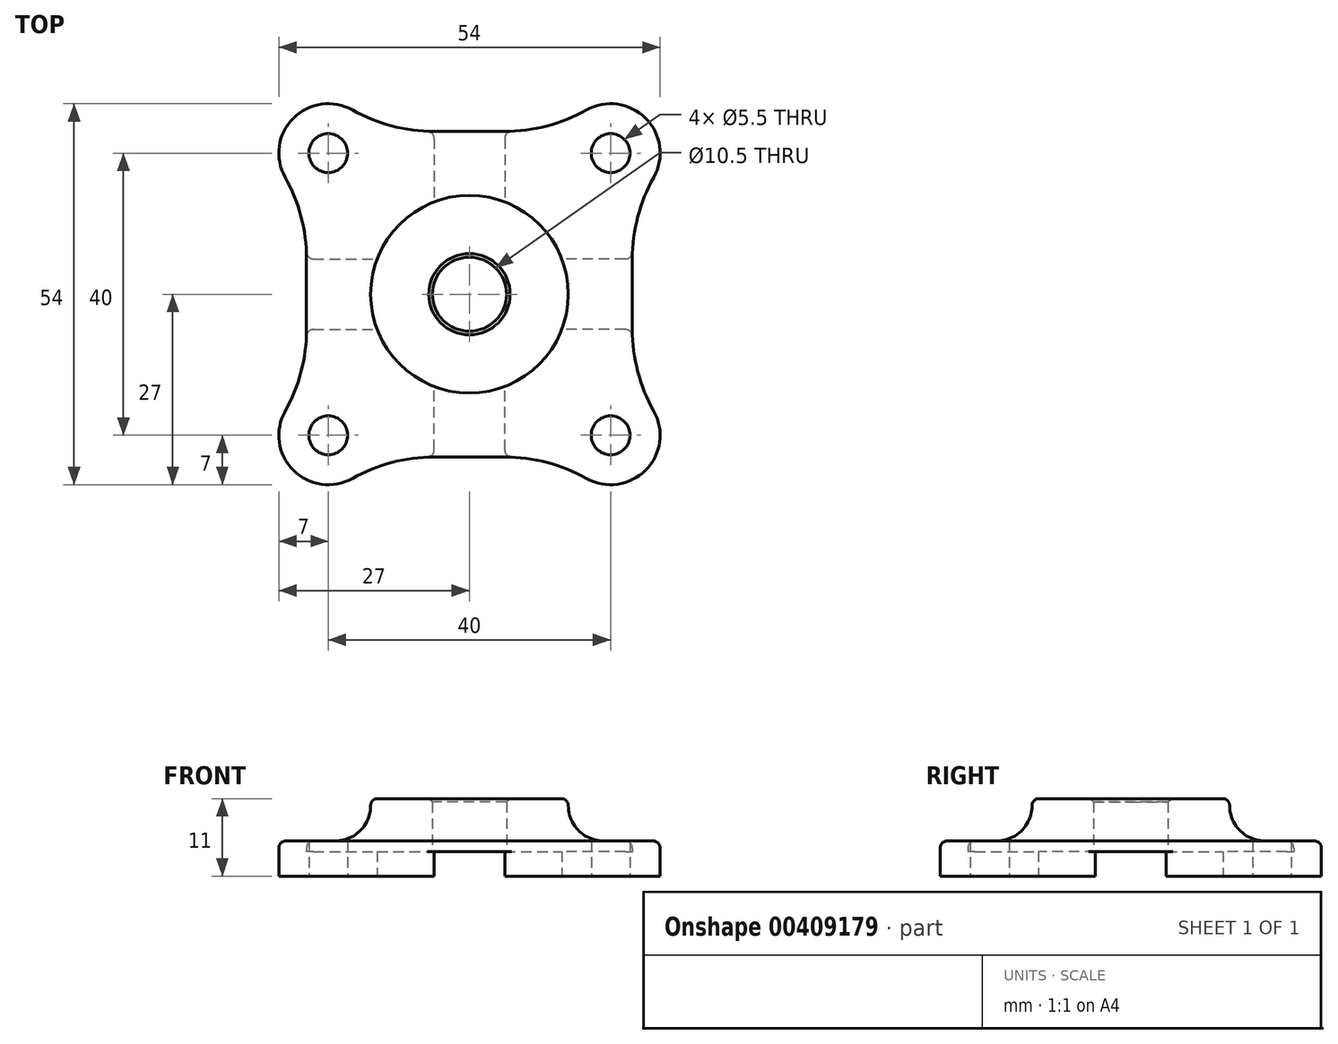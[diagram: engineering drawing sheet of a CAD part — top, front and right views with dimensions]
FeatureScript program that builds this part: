
annotation { "Feature Type Name" : "Feature", "Feature Type Description" : "" }
export const myFeature = defineFeature(function(context is Context, id is Id, definition is map)
    precondition{}
    {
        {
            var Q0;
            Q0=qCreatedBy(makeId("Top.planeOp"),FACE);
            var sketch = newSketch(context, id + "F0", { "sketchPlane" : qUnion([Q0])});
            skCircle(sketch, "E0", {"center": v(0, 0) * mm, "radius": 14 * mm});
            skCircle(sketch, "E1", {"center": v(0, 0) * mm, "radius": 5.25 * mm});
            skCircle(sketch, "E2", {"center": v(0, 0) * mm, "radius": 5 * mm});
            skCircle(sketch, "E3", {"center": v(0, 0) * mm, "radius": 13.5 * mm});
            skCircle(sketch, "E4", {"center": v(-20, 20) * mm, "radius": 2.75 * mm});
            skArc(sketch, "E5", {"start": v(-24.95, 24.95) * mm, "mid": v(-26.93, 20.96) * mm, "end": v(-26.1, 16.57) * mm});
            skLineSegment(sketch, "E6", {"start": v(-23.08, 5) * mm, "end": v(-13.08, 5) * mm});
            skArc(sketch, "E7", {"start": v(-26.1, 16.57) * mm, "mid": v(-23.85, 10.98) * mm, "end": v(-23.08, 5) * mm});
            skLineSegment(sketch, "E8", {"start": v(-20, 20) * mm, "end": v(0, 0) * mm, "construction": true});
            skLineSegment(sketch, "E9", {"start": v(-23.08, 5) * mm, "end": v(-23.08, 0) * mm});
            skArc(sketch, "E10.MirrorCS", {"start": v(-24.95, 24.95) * mm, "mid": v(-20.96, 26.93) * mm, "end": v(-16.57, 26.1) * mm});
            skArc(sketch, "E11.MirrorCS", {"start": v(-16.57, 26.1) * mm, "mid": v(-10.98, 23.85) * mm, "end": v(-5, 23.08) * mm});
            skLineSegment(sketch, "E12.MirrorCS", {"start": v(-5, 23.08) * mm, "end": v(-5, 13.08) * mm});
            skLineSegment(sketch, "E13.MirrorCS", {"start": v(-5, 23.08) * mm, "end": v(0, 23.08) * mm});
            skArc(sketch, "E14.1.0", {"start": v(-26.1, -16.57) * mm, "mid": v(-23.85, -10.98) * mm, "end": v(-23.08, -5) * mm});
            skLineSegment(sketch, "E14.1.1", {"start": v(-5, -23.08) * mm, "end": v(-5, -13.08) * mm});
            skArc(sketch, "E14.1.2", {"start": v(-24.95, -24.95) * mm, "mid": v(-26.93, -20.96) * mm, "end": v(-26.1, -16.57) * mm});
            skArc(sketch, "E14.1.3", {"start": v(-24.95, -24.95) * mm, "mid": v(-20.96, -26.93) * mm, "end": v(-16.57, -26.1) * mm});
            skLineSegment(sketch, "E14.1.4", {"start": v(-5, -23.08) * mm, "end": v(0, -23.08) * mm});
            skCircle(sketch, "E14.1.5", {"center": v(-20, -20) * mm, "radius": 2.75 * mm});
            skLineSegment(sketch, "E14.1.7", {"start": v(-23.08, -5) * mm, "end": v(-23.08, 0) * mm});
            skLineSegment(sketch, "E14.1.8", {"start": v(-23.08, -5) * mm, "end": v(-13.08, -5) * mm});
            skArc(sketch, "E14.1.9", {"start": v(-16.57, -26.1) * mm, "mid": v(-10.98, -23.85) * mm, "end": v(-5, -23.08) * mm});
            skLineSegment(sketch, "E14.1.10", {"start": v(-20, -20) * mm, "end": v(0, 0) * mm, "construction": true});
            skArc(sketch, "E14.2.0", {"start": v(16.57, -26.1) * mm, "mid": v(10.98, -23.85) * mm, "end": v(5, -23.08) * mm});
            skLineSegment(sketch, "E14.2.1", {"start": v(23.08, -5) * mm, "end": v(13.08, -5) * mm});
            skArc(sketch, "E14.2.2", {"start": v(24.95, -24.95) * mm, "mid": v(20.96, -26.93) * mm, "end": v(16.57, -26.1) * mm});
            skArc(sketch, "E14.2.3", {"start": v(24.95, -24.95) * mm, "mid": v(26.93, -20.96) * mm, "end": v(26.1, -16.57) * mm});
            skLineSegment(sketch, "E14.2.4", {"start": v(23.08, -5) * mm, "end": v(23.08, 0) * mm});
            skCircle(sketch, "E14.2.5", {"center": v(20, -20) * mm, "radius": 2.75 * mm});
            skLineSegment(sketch, "E14.2.7", {"start": v(5, -23.08) * mm, "end": v(0, -23.08) * mm});
            skLineSegment(sketch, "E14.2.8", {"start": v(5, -23.08) * mm, "end": v(5, -13.08) * mm});
            skArc(sketch, "E14.2.9", {"start": v(26.1, -16.57) * mm, "mid": v(23.85, -10.98) * mm, "end": v(23.08, -5) * mm});
            skLineSegment(sketch, "E14.2.10", {"start": v(20, -20) * mm, "end": v(0, 0) * mm, "construction": true});
            skArc(sketch, "E14.3.0", {"start": v(26.1, 16.57) * mm, "mid": v(23.85, 10.98) * mm, "end": v(23.08, 5) * mm});
            skLineSegment(sketch, "E14.3.1", {"start": v(5, 23.08) * mm, "end": v(5, 13.08) * mm});
            skArc(sketch, "E14.3.2", {"start": v(24.95, 24.95) * mm, "mid": v(26.93, 20.96) * mm, "end": v(26.1, 16.57) * mm});
            skArc(sketch, "E14.3.3", {"start": v(24.95, 24.95) * mm, "mid": v(20.96, 26.93) * mm, "end": v(16.57, 26.1) * mm});
            skLineSegment(sketch, "E14.3.4", {"start": v(5, 23.08) * mm, "end": v(0, 23.08) * mm});
            skCircle(sketch, "E14.3.5", {"center": v(20, 20) * mm, "radius": 2.75 * mm});
            skLineSegment(sketch, "E14.3.7", {"start": v(23.08, 5) * mm, "end": v(23.08, 0) * mm});
            skLineSegment(sketch, "E14.3.8", {"start": v(23.08, 5) * mm, "end": v(13.08, 5) * mm});
            skArc(sketch, "E14.3.9", {"start": v(16.57, 26.1) * mm, "mid": v(10.98, 23.85) * mm, "end": v(5, 23.08) * mm});
            skLineSegment(sketch, "E14.3.10", {"start": v(20, 20) * mm, "end": v(0, 0) * mm, "construction": true});
            skSolve(sketch);
        }
        {
            var Q0;
            {var subQ0=sQuery(id+"F0.wireOp",EDGE,"E14.2.1");Q0=makeQuery(id+"F0.imprint","IMPRINT",FACE,{"disambiguationData":[TD([[makeQuery(id+"F0.imprint","IMPRINT",EDGE,{"derivedFrom":subQ0}),-1.0]])]});}
            var Q1;
            Q1=makeQuery(id+"F0.imprint","IMPRINT",FACE,{"disambiguationData":[TD([[makeQuery(id+"F0.imprint","IMPRINT",EDGE,{"derivedFrom":sQuery(id+"F0.wireOp",EDGE,"E14.3.0")}),-1.0]])]});
            var Q2;
            Q2=makeQuery(id+"F0.imprint","IMPRINT",FACE,{"disambiguationData":[TD([[makeQuery(id+"F0.imprint","IMPRINT",EDGE,{"derivedFrom":sQuery(id+"F0.wireOp",EDGE,"E14.2.0")}),-1.0]])]});
            var Q3;
            Q3=makeQuery(id+"F0.imprint","IMPRINT",FACE,{"disambiguationData":[TD([[makeQuery(id+"F0.imprint","IMPRINT",EDGE,{"derivedFrom":sQuery(id+"F0.wireOp",EDGE,"E4")}),-1.0]])]});
            var Q4;
            Q4=makeQuery(id+"F0.imprint","IMPRINT",FACE,{"disambiguationData":[TD([[makeQuery(id+"F0.imprint","IMPRINT",EDGE,{"derivedFrom":sQuery(id+"F0.wireOp",EDGE,"E3")}),-1.0]])]});
            var Q5;
            Q5=makeQuery(id+"F0.imprint","IMPRINT",FACE,{"disambiguationData":[TD([[makeQuery(id+"F0.imprint","IMPRINT",EDGE,{"derivedFrom":sQuery(id+"F0.wireOp",EDGE,"E14.1.0")}),-1.0]])]});
            var Q6;
            {var subQ0=sQuery(id+"F0.wireOp",EDGE,"E14.1.1");Q6=makeQuery(id+"F0.imprint","IMPRINT",FACE,{"disambiguationData":[TD([[makeQuery(id+"F0.imprint","IMPRINT",EDGE,{"derivedFrom":subQ0}),-1.0]])]});}
            var Q7;
            Q7=makeQuery(id+"F0.imprint","IMPRINT",FACE,{"disambiguationData":[TD([[makeQuery(id+"F0.imprint","IMPRINT",EDGE,{"derivedFrom":sQuery(id+"F0.wireOp",EDGE,"E1")}),-1.0]])]});
            var Q8;
            {var subQ0=sQuery(id+"F0.wireOp",EDGE,"E6");Q8=makeQuery(id+"F0.imprint","IMPRINT",FACE,{"disambiguationData":[TD([[makeQuery(id+"F0.imprint","IMPRINT",EDGE,{"derivedFrom":subQ0}),-1.0]])]});}
            var Q9;
            {var subQ1=sQuery(id+"F0.wireOp",EDGE,"E12.MirrorCS");Q9=makeQuery(id+"F0.imprint","IMPRINT",FACE,{"disambiguationData":[TD([[makeQuery(id+"F0.imprint","IMPRINT",EDGE,{"derivedFrom":subQ1}),1.0]])]});}
            extrude(context, id + "F1", {"entities" : qUnion([Q0, Q1, Q2, Q3, Q4, Q5, Q6, Q7, Q8, Q9]), "depth" : 3 * mm, "offsetDistance" : 25 * mm});
        }
        {
            var Q0;
            Q0=makeQuery(id+"F0.imprint","IMPRINT",FACE,{"disambiguationData":[TD([[makeQuery(id+"F0.imprint","IMPRINT",EDGE,{"derivedFrom":sQuery(id+"F0.wireOp",EDGE,"E0")}),1.0]])]});
            var Q1;
            Q1=makeQuery(id+"F0.imprint","IMPRINT",FACE,{"disambiguationData":[TD([[makeQuery(id+"F0.imprint","IMPRINT",EDGE,{"derivedFrom":sQuery(id+"F0.wireOp",EDGE,"E1")}),-1.0]])]});
            extrude(context, id + "F2", {"entities" : qUnion([Q0, Q1]), "operationType" : NewBodyOperationType.ADD, "depth" : 9 * mm});
        }
        {
            var Q0;
            Q0=makeQuery(id+"F0.imprint","IMPRINT",FACE,{"disambiguationData":[TD([[makeQuery(id+"F0.imprint","IMPRINT",EDGE,{"derivedFrom":sQuery(id+"F0.wireOp",EDGE,"E1")}),-1.0]])]});
            var Q1;
            {var subQ0=sQuery(id+"F0.wireOp",EDGE,"5FznAjd5-Rlev-DzMA-E21E-VBbVsZXluKNu");Q1=makeQuery(id+"F0.imprint","IMPRINT",FACE,{"disambiguationData":[TD([[makeQuery(id+"F0.imprint","IMPRINT",EDGE,{"derivedFrom":subQ0}),1.0]])]});}
            var Q2;
            Q2=makeQuery(id+"F0.imprint","IMPRINT",FACE,{"disambiguationData":[TD([[makeQuery(id+"F0.imprint","IMPRINT",EDGE,{"derivedFrom":sQuery(id+"F0.wireOp",EDGE,"E3")}),-1.0]])]});
            var Q3;
            {var subQ1=sQuery(id+"F0.wireOp",EDGE,"bf5245d6-79ee-4a8b-a03c-ecbf48f2092a0.MirrorCS");Q3=makeQuery(id+"F0.imprint","IMPRINT",FACE,{"disambiguationData":[TD([[makeQuery(id+"F0.imprint","IMPRINT",EDGE,{"derivedFrom":subQ1}),-1.0]])]});}
            var Q4;
            {var subQ0=sQuery(id+"F0.wireOp",EDGE,"E14.1.1");Q4=makeQuery(id+"F0.imprint","IMPRINT",FACE,{"disambiguationData":[TD([[makeQuery(id+"F0.imprint","IMPRINT",EDGE,{"derivedFrom":subQ0}),-1.0]])]});}
            var Q5;
            {var subQ0=sQuery(id+"F0.wireOp",EDGE,"E6");Q5=makeQuery(id+"F0.imprint","IMPRINT",FACE,{"disambiguationData":[TD([[makeQuery(id+"F0.imprint","IMPRINT",EDGE,{"derivedFrom":subQ0}),-1.0]])]});}
            var Q6;
            {var subQ0=sQuery(id+"F0.wireOp",EDGE,"E14.2.1");Q6=makeQuery(id+"F0.imprint","IMPRINT",FACE,{"disambiguationData":[TD([[makeQuery(id+"F0.imprint","IMPRINT",EDGE,{"derivedFrom":subQ0}),-1.0]])]});}
            var Q7;
            {var subQ1=sQuery(id+"F0.wireOp",EDGE,"E12.MirrorCS");Q7=makeQuery(id+"F0.imprint","IMPRINT",FACE,{"disambiguationData":[TD([[makeQuery(id+"F0.imprint","IMPRINT",EDGE,{"derivedFrom":subQ1}),1.0]])]});}
            extrude(context, id + "F3", {"entities" : qUnion([Q0, Q1, Q2, Q3, Q4, Q5, Q6, Q7]), "operationType" : NewBodyOperationType.REMOVE, "depth" : 1.5 * mm, "offsetDistance" : 25 * mm});
        }
        {
            var Q0;
            Q0=makeQuery(id+"F0.imprint","IMPRINT",FACE,{"disambiguationData":[TD([[makeQuery(id+"F0.imprint","IMPRINT",EDGE,{"derivedFrom":sQuery(id+"F0.wireOp",EDGE,"E14.1.0")}),-1.0]])]});
            var Q1;
            {var subQ0=sQuery(id+"F0.wireOp",EDGE,"E14.1.1");Q1=makeQuery(id+"F0.imprint","IMPRINT",FACE,{"disambiguationData":[TD([[makeQuery(id+"F0.imprint","IMPRINT",EDGE,{"derivedFrom":subQ0}),-1.0]])]});}
            var Q2;
            Q2=makeQuery(id+"F0.imprint","IMPRINT",FACE,{"disambiguationData":[TD([[makeQuery(id+"F0.imprint","IMPRINT",EDGE,{"derivedFrom":sQuery(id+"F0.wireOp",EDGE,"E14.2.0")}),-1.0]])]});
            var Q3;
            {var subQ0=sQuery(id+"F0.wireOp",EDGE,"E14.2.1");Q3=makeQuery(id+"F0.imprint","IMPRINT",FACE,{"disambiguationData":[TD([[makeQuery(id+"F0.imprint","IMPRINT",EDGE,{"derivedFrom":subQ0}),-1.0]])]});}
            var Q4;
            Q4=makeQuery(id+"F0.imprint","IMPRINT",FACE,{"disambiguationData":[TD([[makeQuery(id+"F0.imprint","IMPRINT",EDGE,{"derivedFrom":sQuery(id+"F0.wireOp",EDGE,"E14.3.0")}),-1.0]])]});
            var Q5;
            {var subQ1=sQuery(id+"F0.wireOp",EDGE,"E12.MirrorCS");Q5=makeQuery(id+"F0.imprint","IMPRINT",FACE,{"disambiguationData":[TD([[makeQuery(id+"F0.imprint","IMPRINT",EDGE,{"derivedFrom":subQ1}),1.0]])]});}
            var Q6;
            Q6=makeQuery(id+"F0.imprint","IMPRINT",FACE,{"disambiguationData":[TD([[makeQuery(id+"F0.imprint","IMPRINT",EDGE,{"derivedFrom":sQuery(id+"F0.wireOp",EDGE,"E4")}),-1.0]])]});
            var Q7;
            {var subQ0=sQuery(id+"F0.wireOp",EDGE,"E6");Q7=makeQuery(id+"F0.imprint","IMPRINT",FACE,{"disambiguationData":[TD([[makeQuery(id+"F0.imprint","IMPRINT",EDGE,{"derivedFrom":subQ0}),-1.0]])]});}
            var Q8;
            Q8=makeQuery(id+"F0.imprint","IMPRINT",FACE,{"disambiguationData":[TD([[makeQuery(id+"F0.imprint","IMPRINT",EDGE,{"derivedFrom":sQuery(id+"F0.wireOp",EDGE,"E3")}),-1.0]])]});
            var Q9;
            Q9=makeQuery(id+"F0.imprint","IMPRINT",FACE,{"disambiguationData":[TD([[makeQuery(id+"F0.imprint","IMPRINT",EDGE,{"derivedFrom":sQuery(id+"F0.wireOp",EDGE,"E1")}),-1.0]])]});
            var Q10;
            Q10=makeQuery(id+"F0.imprint","IMPRINT",FACE,{"disambiguationData":[TD([[makeQuery(id+"F0.imprint","IMPRINT",EDGE,{"derivedFrom":sQuery(id+"F0.wireOp",EDGE,"E1")}),1.0]])]});
            var Q11;
            Q11=makeQuery(id+"F0.imprint","IMPRINT",FACE,{"disambiguationData":[TD([[makeQuery(id+"F0.imprint","IMPRINT",EDGE,{"derivedFrom":sQuery(id+"F0.wireOp",EDGE,"E2")}),1.0]])]});
            extrude(context, id + "F4", {"entities" : qUnion([Q0, Q1, Q2, Q3, Q4, Q5, Q6, Q7, Q8, Q9, Q10, Q11]), "oppositeDirection" : true, "depth" : 3 * mm, "offsetDistance" : 25 * mm});
        }
        {
            var Q0;
            {var subQ0=sQuery(id+"F0.wireOp",EDGE,"E6");Q0=makeQuery(id+"F0.imprint","IMPRINT",FACE,{"disambiguationData":[TD([[makeQuery(id+"F0.imprint","IMPRINT",EDGE,{"derivedFrom":subQ0}),-1.0]])]});}
            var Q1;
            Q1=makeQuery(id+"F0.imprint","IMPRINT",FACE,{"disambiguationData":[TD([[makeQuery(id+"F0.imprint","IMPRINT",EDGE,{"derivedFrom":sQuery(id+"F0.wireOp",EDGE,"E3")}),-1.0]])]});
            var Q2;
            {var subQ1=sQuery(id+"F0.wireOp",EDGE,"E12.MirrorCS");Q2=makeQuery(id+"F0.imprint","IMPRINT",FACE,{"disambiguationData":[TD([[makeQuery(id+"F0.imprint","IMPRINT",EDGE,{"derivedFrom":subQ1}),1.0]])]});}
            var Q3;
            {var subQ0=sQuery(id+"F0.wireOp",EDGE,"E14.2.1");Q3=makeQuery(id+"F0.imprint","IMPRINT",FACE,{"disambiguationData":[TD([[makeQuery(id+"F0.imprint","IMPRINT",EDGE,{"derivedFrom":subQ0}),-1.0]])]});}
            var Q4;
            {var subQ0=sQuery(id+"F0.wireOp",EDGE,"E14.1.1");Q4=makeQuery(id+"F0.imprint","IMPRINT",FACE,{"disambiguationData":[TD([[makeQuery(id+"F0.imprint","IMPRINT",EDGE,{"derivedFrom":subQ0}),-1.0]])]});}
            extrude(context, id + "F5", {"entities" : qUnion([Q0, Q1, Q2, Q3, Q4]), "operationType" : NewBodyOperationType.REMOVE, "oppositeDirection" : true, "depth" : 1.5 * mm, "offsetDistance" : 25 * mm});
        }
        {
            var Q0;
            Q0=makeQuery(id+"F2.opExtrude","CAP_EDGE",EDGE,{"disambiguationData":[OSD([sQuery(id+"F0.wireOp",EDGE,"E1")])],"isStart":false});
            var Q1;
            Q1=makeQuery(id+"F1.opExtrude","CAP_EDGE",EDGE,{"disambiguationData":[OSD([sQuery(id+"F0.wireOp",EDGE,"CR5xfrm7-slQB-9y9x-49ej-DvTKbvRHMWAN")])],"isStart":false});
            var Q2;
            Q2=makeQuery(id+"F1.opExtrude","CAP_EDGE",EDGE,{"disambiguationData":[OSD([sQuery(id+"F0.wireOp",EDGE,"M7DjQCVk-RdmV-3Hag-MnrL-rbCDdXIXaqB2")])],"isStart":false});
            var Q3;
            Q3=makeQuery(id+"F1.opExtrude","CAP_EDGE",EDGE,{"disambiguationData":[OSD([sQuery(id+"F0.wireOp",EDGE,"1c0b76fe-b687-46b7-8a7e-c5c0399cf78e0.MirrorC")])],"isStart":false});
            var Q4;
            Q4=makeQuery(id+"F1.opExtrude","CAP_EDGE",EDGE,{"disambiguationData":[OSD([sQuery(id+"F0.wireOp",EDGE,"bdfab768-ba76-4727-b505-0cc44eabfd0a0.MirrorC")])],"isStart":false});
            var Q5;
            Q5=makeQuery(id+"F1.opExtrude","CAP_EDGE",EDGE,{"disambiguationData":[OSD([sQuery(id+"F0.wireOp",EDGE,"bfb17f77-1127-425d-aafc-ff64732babe76.MirrorC")])],"isStart":false});
            chamfer(context, id + "F6", {"entities" : qUnion([Q0, Q1, Q2, Q3, Q4, Q5]), "width" : 0.5 * mm, "tangentPropagation" : true});
        }
        {
            var Q0;
            Q0=makeQuery(id+"F2.boolean.opBoolean","INTERSECT",EDGE,{"derivedFrom":[makeQuery(id+"F1.opExtrude","CAP_FACE",FACE,{"disambiguationData":[OSD([sQuery(id+"F0.wireOp",EDGE,"E1"),sQuery(id+"F0.wireOp",EDGE,"E4"),sQuery(id+"F0.wireOp",EDGE,"E5"),sQuery(id+"F0.wireOp",EDGE,"E7"),sQuery(id+"F0.wireOp",EDGE,"E9"),sQuery(id+"F0.wireOp",EDGE,"E10.MirrorCS"),sQuery(id+"F0.wireOp",EDGE,"E11.MirrorCS"),sQuery(id+"F0.wireOp",EDGE,"E13.MirrorCS"),sQuery(id+"F0.wireOp",EDGE,"E14.1.0"),sQuery(id+"F0.wireOp",EDGE,"E14.1.2"),sQuery(id+"F0.wireOp",EDGE,"E14.1.3"),sQuery(id+"F0.wireOp",EDGE,"E14.1.4"),sQuery(id+"F0.wireOp",EDGE,"E14.1.5"),sQuery(id+"F0.wireOp",EDGE,"E14.1.7"),sQuery(id+"F0.wireOp",EDGE,"E14.1.9"),sQuery(id+"F0.wireOp",EDGE,"E14.2.0"),sQuery(id+"F0.wireOp",EDGE,"E14.2.2"),sQuery(id+"F0.wireOp",EDGE,"E14.2.3"),sQuery(id+"F0.wireOp",EDGE,"E14.2.4"),sQuery(id+"F0.wireOp",EDGE,"E14.2.5"),sQuery(id+"F0.wireOp",EDGE,"E14.2.7"),sQuery(id+"F0.wireOp",EDGE,"E14.2.9"),sQuery(id+"F0.wireOp",EDGE,"E14.3.0"),sQuery(id+"F0.wireOp",EDGE,"E14.3.2"),sQuery(id+"F0.wireOp",EDGE,"E14.3.3"),sQuery(id+"F0.wireOp",EDGE,"E14.3.4"),sQuery(id+"F0.wireOp",EDGE,"E14.3.5"),sQuery(id+"F0.wireOp",EDGE,"E14.3.7"),sQuery(id+"F0.wireOp",EDGE,"E14.3.9")])],"isStart":false}),makeQuery(id+"F2.opExtrude","SWEPT_FACE",FACE,{"disambiguationData":[OSD([sQuery(id+"F0.wireOp",EDGE,"E0")])]})]});
            fillet(context, id + "F7", {"entities" : qUnion([Q0]), "radius" : 5 * mm, "tangentPropagation" : true, "allowEdgeOverflow" : false});
        }
        {
            var Q0;
            {var subQ0=sQuery(id+"F0.wireOp",EDGE,"E0");Q0=makeQuery(id+"F5.boolean.opBoolean","COPY",EDGE,{"derivedFrom":makeQuery(id+"F5.opExtrude","CAP_EDGE",EDGE,{"disambiguationData":[OSD([subQ0]),TDD([makeQuery(id+"F0.imprint","IMPRINT",EDGE,{"disambiguationData":[TD([[makeQuery(id+"F0.imprint","INTERSECT",VERTEX,{"derivedFrom":[subQ0,sQuery(id+"F0.wireOp",EDGE,"E6")]}),1.0]])],"derivedFrom":subQ0})])],"isStart":false})});}
            var Q1;
            {var subQ0=sQuery(id+"F0.wireOp",EDGE,"E0");Q1=makeQuery(id+"F5.boolean.opBoolean","COPY",EDGE,{"derivedFrom":makeQuery(id+"F5.opExtrude","CAP_EDGE",EDGE,{"disambiguationData":[OSD([subQ0]),TDD([makeQuery(id+"F0.imprint","IMPRINT",EDGE,{"disambiguationData":[TD([[makeQuery(id+"F0.imprint","INTERSECT",VERTEX,{"derivedFrom":[subQ0,sQuery(id+"F0.wireOp",EDGE,"E14.1.1")]}),1.0]])],"derivedFrom":subQ0})])],"isStart":false})});}
            var Q2;
            {var subQ0=sQuery(id+"F0.wireOp",EDGE,"E0");Q2=makeQuery(id+"F5.boolean.opBoolean","COPY",EDGE,{"derivedFrom":makeQuery(id+"F5.opExtrude","CAP_EDGE",EDGE,{"disambiguationData":[OSD([subQ0]),TDD([makeQuery(id+"F0.imprint","IMPRINT",EDGE,{"disambiguationData":[TD([[makeQuery(id+"F0.imprint","INTERSECT",VERTEX,{"derivedFrom":[subQ0,sQuery(id+"F0.wireOp",EDGE,"E14.2.1")]}),1.0]])],"derivedFrom":subQ0})])],"isStart":false})});}
            var Q3;
            {var subQ0=sQuery(id+"F0.wireOp",EDGE,"E0");Q3=makeQuery(id+"F5.boolean.opBoolean","COPY",EDGE,{"derivedFrom":makeQuery(id+"F5.opExtrude","CAP_EDGE",EDGE,{"disambiguationData":[OSD([subQ0]),TDD([makeQuery(id+"F0.imprint","IMPRINT",EDGE,{"disambiguationData":[TD([[makeQuery(id+"F0.imprint","INTERSECT",VERTEX,{"derivedFrom":[subQ0,sQuery(id+"F0.wireOp",EDGE,"E14.3.1")]}),1.0]])],"derivedFrom":subQ0})])],"isStart":false})});}
            var Q4;
            {var subQ0=sQuery(id+"F0.wireOp",EDGE,"E14.2.9");var subQ1=sQuery(id+"F0.wireOp",EDGE,"E14.2.4");var subQ2=sQuery(id+"F0.wireOp",EDGE,"E14.2.1");Q4=makeQuery(id+"F3.boolean.opBoolean","MERGE",EDGE,{"derivedFrom":[makeQuery(id+"F1.opExtrude","SWEPT_EDGE",EDGE,{"disambiguationData":[OSD([subQ2,subQ1,subQ0])]}),makeQuery(id+"F3.opExtrude","SWEPT_EDGE",EDGE,{"disambiguationData":[OSD([subQ2,subQ1,subQ0])]})]});}
            var Q5;
            {var subQ0=sQuery(id+"F0.wireOp",EDGE,"E14.2.9");var subQ1=sQuery(id+"F0.wireOp",EDGE,"E14.2.4");var subQ2=sQuery(id+"F0.wireOp",EDGE,"E14.2.1");Q5=makeQuery(id+"F5.boolean.opBoolean","MERGE",EDGE,{"derivedFrom":[makeQuery(id+"F4.opExtrude","SWEPT_EDGE",EDGE,{"disambiguationData":[OSD([subQ2,subQ1,subQ0])]}),makeQuery(id+"F5.opExtrude","SWEPT_EDGE",EDGE,{"disambiguationData":[OSD([subQ2,subQ1,subQ0])]})]});}
            var Q6;
            {var subQ0=sQuery(id+"F0.wireOp",EDGE,"E14.3.8");var subQ1=sQuery(id+"F0.wireOp",EDGE,"E14.3.7");var subQ2=sQuery(id+"F0.wireOp",EDGE,"E14.3.0");Q6=makeQuery(id+"F5.boolean.opBoolean","MERGE",EDGE,{"derivedFrom":[makeQuery(id+"F4.opExtrude","SWEPT_EDGE",EDGE,{"disambiguationData":[OSD([subQ2,subQ1,subQ0])]}),makeQuery(id+"F5.opExtrude","SWEPT_EDGE",EDGE,{"disambiguationData":[OSD([subQ2,subQ1,subQ0])]})]});}
            var Q7;
            {var subQ0=sQuery(id+"F0.wireOp",EDGE,"E14.3.8");var subQ1=sQuery(id+"F0.wireOp",EDGE,"E14.3.7");var subQ2=sQuery(id+"F0.wireOp",EDGE,"E14.3.0");Q7=makeQuery(id+"F3.boolean.opBoolean","MERGE",EDGE,{"derivedFrom":[makeQuery(id+"F1.opExtrude","SWEPT_EDGE",EDGE,{"disambiguationData":[OSD([subQ2,subQ1,subQ0])]}),makeQuery(id+"F3.opExtrude","SWEPT_EDGE",EDGE,{"disambiguationData":[OSD([subQ2,subQ1,subQ0])]})]});}
            var Q8;
            {var subQ0=sQuery(id+"F0.wireOp",EDGE,"E14.3.9");var subQ1=sQuery(id+"F0.wireOp",EDGE,"E14.3.4");var subQ2=sQuery(id+"F0.wireOp",EDGE,"E14.3.1");Q8=makeQuery(id+"F3.boolean.opBoolean","MERGE",EDGE,{"derivedFrom":[makeQuery(id+"F1.opExtrude","SWEPT_EDGE",EDGE,{"disambiguationData":[OSD([subQ2,subQ1,subQ0])]}),makeQuery(id+"F3.opExtrude","SWEPT_EDGE",EDGE,{"disambiguationData":[OSD([subQ2,subQ1,subQ0])]})]});}
            var Q9;
            {var subQ0=sQuery(id+"F0.wireOp",EDGE,"E14.3.9");var subQ1=sQuery(id+"F0.wireOp",EDGE,"E14.3.4");var subQ2=sQuery(id+"F0.wireOp",EDGE,"E14.3.1");Q9=makeQuery(id+"F5.boolean.opBoolean","MERGE",EDGE,{"derivedFrom":[makeQuery(id+"F4.opExtrude","SWEPT_EDGE",EDGE,{"disambiguationData":[OSD([subQ2,subQ1,subQ0])]}),makeQuery(id+"F5.opExtrude","SWEPT_EDGE",EDGE,{"disambiguationData":[OSD([subQ2,subQ1,subQ0])]})]});}
            var Q10;
            {var subQ0=sQuery(id+"F0.wireOp",EDGE,"E13.MirrorCS");var subQ1=sQuery(id+"F0.wireOp",EDGE,"E12.MirrorCS");var subQ2=sQuery(id+"F0.wireOp",EDGE,"E11.MirrorCS");Q10=makeQuery(id+"F3.boolean.opBoolean","MERGE",EDGE,{"derivedFrom":[makeQuery(id+"F1.opExtrude","SWEPT_EDGE",EDGE,{"disambiguationData":[OSD([subQ2,subQ1,subQ0])]}),makeQuery(id+"F3.opExtrude","SWEPT_EDGE",EDGE,{"disambiguationData":[OSD([subQ2,subQ1,subQ0])]})]});}
            var Q11;
            {var subQ0=sQuery(id+"F0.wireOp",EDGE,"E13.MirrorCS");var subQ1=sQuery(id+"F0.wireOp",EDGE,"E12.MirrorCS");var subQ2=sQuery(id+"F0.wireOp",EDGE,"E11.MirrorCS");Q11=makeQuery(id+"F5.boolean.opBoolean","MERGE",EDGE,{"derivedFrom":[makeQuery(id+"F4.opExtrude","SWEPT_EDGE",EDGE,{"disambiguationData":[OSD([subQ2,subQ1,subQ0])]}),makeQuery(id+"F5.opExtrude","SWEPT_EDGE",EDGE,{"disambiguationData":[OSD([subQ2,subQ1,subQ0])]})]});}
            var Q12;
            {var subQ0=sQuery(id+"F0.wireOp",EDGE,"E9");var subQ1=sQuery(id+"F0.wireOp",EDGE,"E7");var subQ2=sQuery(id+"F0.wireOp",EDGE,"E6");Q12=makeQuery(id+"F3.boolean.opBoolean","MERGE",EDGE,{"derivedFrom":[makeQuery(id+"F1.opExtrude","SWEPT_EDGE",EDGE,{"disambiguationData":[OSD([subQ2,subQ1,subQ0])]}),makeQuery(id+"F3.opExtrude","SWEPT_EDGE",EDGE,{"disambiguationData":[OSD([subQ2,subQ1,subQ0])]})]});}
            var Q13;
            {var subQ0=sQuery(id+"F0.wireOp",EDGE,"E9");var subQ1=sQuery(id+"F0.wireOp",EDGE,"E7");var subQ2=sQuery(id+"F0.wireOp",EDGE,"E6");Q13=makeQuery(id+"F5.boolean.opBoolean","MERGE",EDGE,{"derivedFrom":[makeQuery(id+"F4.opExtrude","SWEPT_EDGE",EDGE,{"disambiguationData":[OSD([subQ2,subQ1,subQ0])]}),makeQuery(id+"F5.opExtrude","SWEPT_EDGE",EDGE,{"disambiguationData":[OSD([subQ2,subQ1,subQ0])]})]});}
            var Q14;
            {var subQ0=sQuery(id+"F0.wireOp",EDGE,"E14.1.8");var subQ1=sQuery(id+"F0.wireOp",EDGE,"E14.1.7");var subQ2=sQuery(id+"F0.wireOp",EDGE,"E14.1.0");Q14=makeQuery(id+"F3.boolean.opBoolean","MERGE",EDGE,{"derivedFrom":[makeQuery(id+"F1.opExtrude","SWEPT_EDGE",EDGE,{"disambiguationData":[OSD([subQ2,subQ1,subQ0])]}),makeQuery(id+"F3.opExtrude","SWEPT_EDGE",EDGE,{"disambiguationData":[OSD([subQ2,subQ1,subQ0])]})]});}
            var Q15;
            {var subQ0=sQuery(id+"F0.wireOp",EDGE,"E14.1.8");var subQ1=sQuery(id+"F0.wireOp",EDGE,"E14.1.7");var subQ2=sQuery(id+"F0.wireOp",EDGE,"E14.1.0");Q15=makeQuery(id+"F5.boolean.opBoolean","MERGE",EDGE,{"derivedFrom":[makeQuery(id+"F4.opExtrude","SWEPT_EDGE",EDGE,{"disambiguationData":[OSD([subQ2,subQ1,subQ0])]}),makeQuery(id+"F5.opExtrude","SWEPT_EDGE",EDGE,{"disambiguationData":[OSD([subQ2,subQ1,subQ0])]})]});}
            var Q16;
            {var subQ0=sQuery(id+"F0.wireOp",EDGE,"E14.1.9");var subQ1=sQuery(id+"F0.wireOp",EDGE,"E14.1.4");var subQ2=sQuery(id+"F0.wireOp",EDGE,"E14.1.1");Q16=makeQuery(id+"F3.boolean.opBoolean","MERGE",EDGE,{"derivedFrom":[makeQuery(id+"F1.opExtrude","SWEPT_EDGE",EDGE,{"disambiguationData":[OSD([subQ2,subQ1,subQ0])]}),makeQuery(id+"F3.opExtrude","SWEPT_EDGE",EDGE,{"disambiguationData":[OSD([subQ2,subQ1,subQ0])]})]});}
            var Q17;
            {var subQ0=sQuery(id+"F0.wireOp",EDGE,"E14.1.9");var subQ1=sQuery(id+"F0.wireOp",EDGE,"E14.1.4");var subQ2=sQuery(id+"F0.wireOp",EDGE,"E14.1.1");Q17=makeQuery(id+"F5.boolean.opBoolean","MERGE",EDGE,{"derivedFrom":[makeQuery(id+"F4.opExtrude","SWEPT_EDGE",EDGE,{"disambiguationData":[OSD([subQ2,subQ1,subQ0])]}),makeQuery(id+"F5.opExtrude","SWEPT_EDGE",EDGE,{"disambiguationData":[OSD([subQ2,subQ1,subQ0])]})]});}
            var Q18;
            {var subQ0=sQuery(id+"F0.wireOp",EDGE,"E14.2.8");var subQ1=sQuery(id+"F0.wireOp",EDGE,"E14.2.7");var subQ2=sQuery(id+"F0.wireOp",EDGE,"E14.2.0");Q18=makeQuery(id+"F3.boolean.opBoolean","MERGE",EDGE,{"derivedFrom":[makeQuery(id+"F1.opExtrude","SWEPT_EDGE",EDGE,{"disambiguationData":[OSD([subQ2,subQ1,subQ0])]}),makeQuery(id+"F3.opExtrude","SWEPT_EDGE",EDGE,{"disambiguationData":[OSD([subQ2,subQ1,subQ0])]})]});}
            var Q19;
            {var subQ0=sQuery(id+"F0.wireOp",EDGE,"E14.2.8");var subQ1=sQuery(id+"F0.wireOp",EDGE,"E14.2.7");var subQ2=sQuery(id+"F0.wireOp",EDGE,"E14.2.0");Q19=makeQuery(id+"F5.boolean.opBoolean","MERGE",EDGE,{"derivedFrom":[makeQuery(id+"F4.opExtrude","SWEPT_EDGE",EDGE,{"disambiguationData":[OSD([subQ2,subQ1,subQ0])]}),makeQuery(id+"F5.opExtrude","SWEPT_EDGE",EDGE,{"disambiguationData":[OSD([subQ2,subQ1,subQ0])]})]});}
            var Q20;
            {var subQ0=sQuery(id+"F0.wireOp",EDGE,"E1");var subQ1=sQuery(id+"F0.wireOp",EDGE,"E0");Q20=makeQuery(id+"F7.opFillet","BLEND_EDGE",EDGE,{"blendedFrom":[makeQuery(id+"F2.boolean.opBoolean","INTERSECT",EDGE,{"derivedFrom":[makeQuery(id+"F1.opExtrude","CAP_FACE",FACE,{"disambiguationData":[OSD([subQ0,sQuery(id+"F0.wireOp",EDGE,"E4"),sQuery(id+"F0.wireOp",EDGE,"E5"),sQuery(id+"F0.wireOp",EDGE,"E7"),sQuery(id+"F0.wireOp",EDGE,"E9"),sQuery(id+"F0.wireOp",EDGE,"E10.MirrorCS"),sQuery(id+"F0.wireOp",EDGE,"E11.MirrorCS"),sQuery(id+"F0.wireOp",EDGE,"E13.MirrorCS"),sQuery(id+"F0.wireOp",EDGE,"E14.1.0"),sQuery(id+"F0.wireOp",EDGE,"E14.1.2"),sQuery(id+"F0.wireOp",EDGE,"E14.1.3"),sQuery(id+"F0.wireOp",EDGE,"E14.1.4"),sQuery(id+"F0.wireOp",EDGE,"E14.1.5"),sQuery(id+"F0.wireOp",EDGE,"E14.1.7"),sQuery(id+"F0.wireOp",EDGE,"E14.1.9"),sQuery(id+"F0.wireOp",EDGE,"E14.2.0"),sQuery(id+"F0.wireOp",EDGE,"E14.2.2"),sQuery(id+"F0.wireOp",EDGE,"E14.2.3"),sQuery(id+"F0.wireOp",EDGE,"E14.2.4"),sQuery(id+"F0.wireOp",EDGE,"E14.2.5"),sQuery(id+"F0.wireOp",EDGE,"E14.2.7"),sQuery(id+"F0.wireOp",EDGE,"E14.2.9"),sQuery(id+"F0.wireOp",EDGE,"E14.3.0"),sQuery(id+"F0.wireOp",EDGE,"E14.3.2"),sQuery(id+"F0.wireOp",EDGE,"E14.3.3"),sQuery(id+"F0.wireOp",EDGE,"E14.3.4"),sQuery(id+"F0.wireOp",EDGE,"E14.3.5"),sQuery(id+"F0.wireOp",EDGE,"E14.3.7"),sQuery(id+"F0.wireOp",EDGE,"E14.3.9")])],"isStart":false}),makeQuery(id+"F2.opExtrude","SWEPT_FACE",FACE,{"disambiguationData":[OSD([subQ1])]})]}),makeQuery(id+"F2.opExtrude","CAP_FACE",FACE,{"disambiguationData":[OSD([subQ1,subQ0])],"isStart":false})],"blendedInto":[makeQuery(id+"F2.opExtrude","CAP_FACE",FACE,{"disambiguationData":[OSD([subQ1,subQ0])],"isStart":false})]});}
            var Q21;
            Q21=makeQuery(id+"F1.opExtrude","CAP_EDGE",EDGE,{"disambiguationData":[OSD([sQuery(id+"F0.wireOp",EDGE,"E14.3.2"),sQuery(id+"F0.wireOp",EDGE,"E14.3.3")])],"isStart":false});
            var Q22;
            Q22=makeQuery(id+"F1.opExtrude","CAP_EDGE",EDGE,{"disambiguationData":[OSD([sQuery(id+"F0.wireOp",EDGE,"E5"),sQuery(id+"F0.wireOp",EDGE,"E10.MirrorCS")])],"isStart":false});
            var Q23;
            Q23=makeQuery(id+"F1.opExtrude","CAP_EDGE",EDGE,{"disambiguationData":[OSD([sQuery(id+"F0.wireOp",EDGE,"E14.1.2"),sQuery(id+"F0.wireOp",EDGE,"E14.1.3")])],"isStart":false});
            var Q24;
            Q24=makeQuery(id+"F1.opExtrude","CAP_EDGE",EDGE,{"disambiguationData":[OSD([sQuery(id+"F0.wireOp",EDGE,"E14.2.2"),sQuery(id+"F0.wireOp",EDGE,"E14.2.3")])],"isStart":false});
            var Q25;
            Q25=makeQuery(id+"F1.opExtrude","CAP_EDGE",EDGE,{"disambiguationData":[OSD([sQuery(id+"F0.wireOp",EDGE,"E14.2.4"),sQuery(id+"F0.wireOp",EDGE,"E14.3.7")])],"isStart":false});
            var Q26;
            Q26=makeQuery(id+"F1.opExtrude","CAP_EDGE",EDGE,{"disambiguationData":[OSD([sQuery(id+"F0.wireOp",EDGE,"E13.MirrorCS"),sQuery(id+"F0.wireOp",EDGE,"E14.3.4")])],"isStart":false});
            var Q27;
            Q27=makeQuery(id+"F1.opExtrude","CAP_EDGE",EDGE,{"disambiguationData":[OSD([sQuery(id+"F0.wireOp",EDGE,"E9"),sQuery(id+"F0.wireOp",EDGE,"E14.1.7")])],"isStart":false});
            var Q28;
            Q28=makeQuery(id+"F1.opExtrude","CAP_EDGE",EDGE,{"disambiguationData":[OSD([sQuery(id+"F0.wireOp",EDGE,"E14.1.4"),sQuery(id+"F0.wireOp",EDGE,"E14.2.7")])],"isStart":false});
            var Q29;
            Q29=makeQuery(id+"F2.opExtrude","CAP_EDGE",EDGE,{"disambiguationData":[OSD([sQuery(id+"F0.wireOp",EDGE,"E0")])],"isStart":false});
            fillet(context, id + "F8", {"entities" : qUnion([Q0, Q1, Q2, Q3, Q4, Q5, Q6, Q7, Q8, Q9, Q10, Q11, Q12, Q13, Q14, Q15, Q16, Q17, Q18, Q19, Q20, Q21, Q22, Q23, Q24, Q25, Q26, Q27, Q28, Q29]), "radius" : 1 * mm, "tangentPropagation" : true, "allowEdgeOverflow" : false});
        }
        {
            var Q0;
            Q0=makeQuery(id+"F4.opExtrude","SWEPT_BODY",BODY,{"disambiguationData":[OSD([sQuery(id+"F0.wireOp",EDGE,"E4"),sQuery(id+"F0.wireOp",EDGE,"E5"),sQuery(id+"F0.wireOp",EDGE,"E7"),sQuery(id+"F0.wireOp",EDGE,"E9"),sQuery(id+"F0.wireOp",EDGE,"E10.MirrorCS"),sQuery(id+"F0.wireOp",EDGE,"E11.MirrorCS"),sQuery(id+"F0.wireOp",EDGE,"E13.MirrorCS"),sQuery(id+"F0.wireOp",EDGE,"E14.1.0"),sQuery(id+"F0.wireOp",EDGE,"E14.1.2"),sQuery(id+"F0.wireOp",EDGE,"E14.1.3"),sQuery(id+"F0.wireOp",EDGE,"E14.1.4"),sQuery(id+"F0.wireOp",EDGE,"E14.1.5"),sQuery(id+"F0.wireOp",EDGE,"E14.1.7"),sQuery(id+"F0.wireOp",EDGE,"E14.1.9"),sQuery(id+"F0.wireOp",EDGE,"E14.2.0"),sQuery(id+"F0.wireOp",EDGE,"E14.2.2"),sQuery(id+"F0.wireOp",EDGE,"E14.2.3"),sQuery(id+"F0.wireOp",EDGE,"E14.2.4"),sQuery(id+"F0.wireOp",EDGE,"E14.2.5"),sQuery(id+"F0.wireOp",EDGE,"E14.2.7"),sQuery(id+"F0.wireOp",EDGE,"E14.2.9"),sQuery(id+"F0.wireOp",EDGE,"E14.3.0"),sQuery(id+"F0.wireOp",EDGE,"E14.3.2"),sQuery(id+"F0.wireOp",EDGE,"E14.3.3"),sQuery(id+"F0.wireOp",EDGE,"E14.3.4"),sQuery(id+"F0.wireOp",EDGE,"E14.3.5"),sQuery(id+"F0.wireOp",EDGE,"E14.3.7"),sQuery(id+"F0.wireOp",EDGE,"E14.3.9")])]});
            deleteBodies(context, id + "F9", {"entities" : qUnion([Q0])});
        }
        {
            var Q0;
            {var subQ0=sQuery(id+"F0.wireOp",EDGE,"E14.1.9");var subQ1=sQuery(id+"F0.wireOp",EDGE,"E14.1.5");var subQ3=sQuery(id+"F0.wireOp",EDGE,"E14.1.3");var subQ4=sQuery(id+"F0.wireOp",EDGE,"E14.1.2");var subQ5=sQuery(id+"F0.wireOp",EDGE,"E14.1.0");Q0=makeQuery(id+"F3.boolean.opBoolean","SPLIT",FACE,{"disambiguationData":[TD([makeQuery(id+"F1.opExtrude","SWEPT_FACE",FACE,{"disambiguationData":[OSD([subQ5])]})])],"derivedFrom":makeQuery(id+"F1.opExtrude","CAP_FACE",FACE,{"disambiguationData":[OSD([sQuery(id+"F0.wireOp",EDGE,"E1"),sQuery(id+"F0.wireOp",EDGE,"E4"),sQuery(id+"F0.wireOp",EDGE,"E5"),sQuery(id+"F0.wireOp",EDGE,"E7"),sQuery(id+"F0.wireOp",EDGE,"E9"),sQuery(id+"F0.wireOp",EDGE,"E10.MirrorCS"),sQuery(id+"F0.wireOp",EDGE,"E11.MirrorCS"),sQuery(id+"F0.wireOp",EDGE,"E13.MirrorCS"),subQ5,subQ4,subQ3,sQuery(id+"F0.wireOp",EDGE,"E14.1.4"),subQ1,sQuery(id+"F0.wireOp",EDGE,"E14.1.7"),subQ0,sQuery(id+"F0.wireOp",EDGE,"E14.2.0"),sQuery(id+"F0.wireOp",EDGE,"E14.2.2"),sQuery(id+"F0.wireOp",EDGE,"E14.2.3"),sQuery(id+"F0.wireOp",EDGE,"E14.2.4"),sQuery(id+"F0.wireOp",EDGE,"E14.2.5"),sQuery(id+"F0.wireOp",EDGE,"E14.2.7"),sQuery(id+"F0.wireOp",EDGE,"E14.2.9"),sQuery(id+"F0.wireOp",EDGE,"E14.3.0"),sQuery(id+"F0.wireOp",EDGE,"E14.3.2"),sQuery(id+"F0.wireOp",EDGE,"E14.3.3"),sQuery(id+"F0.wireOp",EDGE,"E14.3.4"),sQuery(id+"F0.wireOp",EDGE,"E14.3.5"),sQuery(id+"F0.wireOp",EDGE,"E14.3.7"),sQuery(id+"F0.wireOp",EDGE,"E14.3.9")])],"isStart":true})});}
            var Q1;
            {var subQ0=sQuery(id+"F0.wireOp",EDGE,"E14.2.9");var subQ1=sQuery(id+"F0.wireOp",EDGE,"E14.2.5");var subQ5=sQuery(id+"F0.wireOp",EDGE,"E14.2.3");var subQ6=sQuery(id+"F0.wireOp",EDGE,"E14.2.2");var subQ7=sQuery(id+"F0.wireOp",EDGE,"E14.2.0");Q1=makeQuery(id+"F3.boolean.opBoolean","SPLIT",FACE,{"disambiguationData":[TD([makeQuery(id+"F1.opExtrude","SWEPT_FACE",FACE,{"disambiguationData":[OSD([subQ7])]})])],"derivedFrom":makeQuery(id+"F1.opExtrude","CAP_FACE",FACE,{"disambiguationData":[OSD([sQuery(id+"F0.wireOp",EDGE,"E1"),sQuery(id+"F0.wireOp",EDGE,"E4"),sQuery(id+"F0.wireOp",EDGE,"E5"),sQuery(id+"F0.wireOp",EDGE,"E7"),sQuery(id+"F0.wireOp",EDGE,"E9"),sQuery(id+"F0.wireOp",EDGE,"E10.MirrorCS"),sQuery(id+"F0.wireOp",EDGE,"E11.MirrorCS"),sQuery(id+"F0.wireOp",EDGE,"E13.MirrorCS"),sQuery(id+"F0.wireOp",EDGE,"E14.1.0"),sQuery(id+"F0.wireOp",EDGE,"E14.1.2"),sQuery(id+"F0.wireOp",EDGE,"E14.1.3"),sQuery(id+"F0.wireOp",EDGE,"E14.1.4"),sQuery(id+"F0.wireOp",EDGE,"E14.1.5"),sQuery(id+"F0.wireOp",EDGE,"E14.1.7"),sQuery(id+"F0.wireOp",EDGE,"E14.1.9"),subQ7,subQ6,subQ5,sQuery(id+"F0.wireOp",EDGE,"E14.2.4"),subQ1,sQuery(id+"F0.wireOp",EDGE,"E14.2.7"),subQ0,sQuery(id+"F0.wireOp",EDGE,"E14.3.0"),sQuery(id+"F0.wireOp",EDGE,"E14.3.2"),sQuery(id+"F0.wireOp",EDGE,"E14.3.3"),sQuery(id+"F0.wireOp",EDGE,"E14.3.4"),sQuery(id+"F0.wireOp",EDGE,"E14.3.5"),sQuery(id+"F0.wireOp",EDGE,"E14.3.7"),sQuery(id+"F0.wireOp",EDGE,"E14.3.9")])],"isStart":true})});}
            var Q2;
            {var subQ0=sQuery(id+"F0.wireOp",EDGE,"E14.3.9");var subQ1=sQuery(id+"F0.wireOp",EDGE,"E14.3.5");var subQ2=sQuery(id+"F0.wireOp",EDGE,"E14.3.3");var subQ3=sQuery(id+"F0.wireOp",EDGE,"E14.3.2");var subQ4=sQuery(id+"F0.wireOp",EDGE,"E14.3.0");Q2=makeQuery(id+"F3.boolean.opBoolean","SPLIT",FACE,{"disambiguationData":[TD([makeQuery(id+"F1.opExtrude","SWEPT_FACE",FACE,{"disambiguationData":[OSD([subQ4])]})])],"derivedFrom":makeQuery(id+"F1.opExtrude","CAP_FACE",FACE,{"disambiguationData":[OSD([sQuery(id+"F0.wireOp",EDGE,"E1"),sQuery(id+"F0.wireOp",EDGE,"E4"),sQuery(id+"F0.wireOp",EDGE,"E5"),sQuery(id+"F0.wireOp",EDGE,"E7"),sQuery(id+"F0.wireOp",EDGE,"E9"),sQuery(id+"F0.wireOp",EDGE,"E10.MirrorCS"),sQuery(id+"F0.wireOp",EDGE,"E11.MirrorCS"),sQuery(id+"F0.wireOp",EDGE,"E13.MirrorCS"),sQuery(id+"F0.wireOp",EDGE,"E14.1.0"),sQuery(id+"F0.wireOp",EDGE,"E14.1.2"),sQuery(id+"F0.wireOp",EDGE,"E14.1.3"),sQuery(id+"F0.wireOp",EDGE,"E14.1.4"),sQuery(id+"F0.wireOp",EDGE,"E14.1.5"),sQuery(id+"F0.wireOp",EDGE,"E14.1.7"),sQuery(id+"F0.wireOp",EDGE,"E14.1.9"),sQuery(id+"F0.wireOp",EDGE,"E14.2.0"),sQuery(id+"F0.wireOp",EDGE,"E14.2.2"),sQuery(id+"F0.wireOp",EDGE,"E14.2.3"),sQuery(id+"F0.wireOp",EDGE,"E14.2.4"),sQuery(id+"F0.wireOp",EDGE,"E14.2.5"),sQuery(id+"F0.wireOp",EDGE,"E14.2.7"),sQuery(id+"F0.wireOp",EDGE,"E14.2.9"),subQ4,subQ3,subQ2,sQuery(id+"F0.wireOp",EDGE,"E14.3.4"),subQ1,sQuery(id+"F0.wireOp",EDGE,"E14.3.7"),subQ0])],"isStart":true})});}
            var Q3;
            {var subQ0=sQuery(id+"F0.wireOp",EDGE,"E11.MirrorCS");var subQ1=sQuery(id+"F0.wireOp",EDGE,"E7");var subQ2=sQuery(id+"F0.wireOp",EDGE,"E10.MirrorCS");var subQ3=sQuery(id+"F0.wireOp",EDGE,"E5");var subQ7=sQuery(id+"F0.wireOp",EDGE,"E4");Q3=makeQuery(id+"F3.boolean.opBoolean","SPLIT",FACE,{"disambiguationData":[TD([makeQuery(id+"F1.opExtrude","SWEPT_FACE",FACE,{"disambiguationData":[OSD([subQ7])]})])],"derivedFrom":makeQuery(id+"F1.opExtrude","CAP_FACE",FACE,{"disambiguationData":[OSD([sQuery(id+"F0.wireOp",EDGE,"E1"),subQ7,subQ3,subQ1,sQuery(id+"F0.wireOp",EDGE,"E9"),subQ2,subQ0,sQuery(id+"F0.wireOp",EDGE,"E13.MirrorCS"),sQuery(id+"F0.wireOp",EDGE,"E14.1.0"),sQuery(id+"F0.wireOp",EDGE,"E14.1.2"),sQuery(id+"F0.wireOp",EDGE,"E14.1.3"),sQuery(id+"F0.wireOp",EDGE,"E14.1.4"),sQuery(id+"F0.wireOp",EDGE,"E14.1.5"),sQuery(id+"F0.wireOp",EDGE,"E14.1.7"),sQuery(id+"F0.wireOp",EDGE,"E14.1.9"),sQuery(id+"F0.wireOp",EDGE,"E14.2.0"),sQuery(id+"F0.wireOp",EDGE,"E14.2.2"),sQuery(id+"F0.wireOp",EDGE,"E14.2.3"),sQuery(id+"F0.wireOp",EDGE,"E14.2.4"),sQuery(id+"F0.wireOp",EDGE,"E14.2.5"),sQuery(id+"F0.wireOp",EDGE,"E14.2.7"),sQuery(id+"F0.wireOp",EDGE,"E14.2.9"),sQuery(id+"F0.wireOp",EDGE,"E14.3.0"),sQuery(id+"F0.wireOp",EDGE,"E14.3.2"),sQuery(id+"F0.wireOp",EDGE,"E14.3.3"),sQuery(id+"F0.wireOp",EDGE,"E14.3.4"),sQuery(id+"F0.wireOp",EDGE,"E14.3.5"),sQuery(id+"F0.wireOp",EDGE,"E14.3.7"),sQuery(id+"F0.wireOp",EDGE,"E14.3.9")])],"isStart":true})});}
            extrude(context, id + "F10", {"entities" : qUnion([Q0, Q1, Q2, Q3]), "operationType" : NewBodyOperationType.ADD, "depth" : 2 * mm, "offsetDistance" : 25 * mm});
        }
    });
